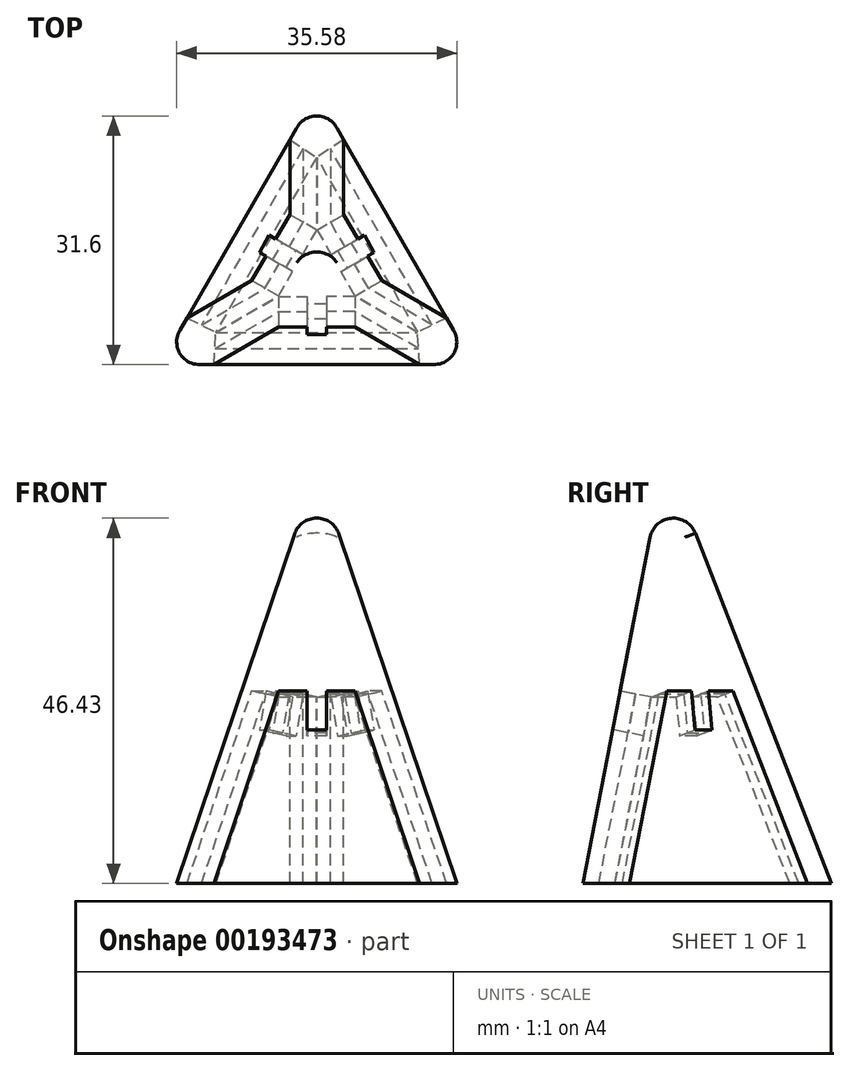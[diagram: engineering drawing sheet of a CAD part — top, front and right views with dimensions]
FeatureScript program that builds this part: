
annotation { "Feature Type Name" : "Feature", "Feature Type Description" : "" }
export const myFeature = defineFeature(function(context is Context, id is Id, definition is map)
    precondition{}
    {
        {
            var Q0;
            Q0=qCreatedBy(makeId("Top.planeOp"),FACE);
            var sketch = newSketch(context, id + "F13", { "sketchPlane" : qUnion([Q0])});
            skLineSegment(sketch, "E0", {"start": v(0, 21.94) * mm, "end": v(-19, -10.97) * mm, "construction": true});
            skLineSegment(sketch, "E1", {"start": v(-19, -10.97) * mm, "end": v(19, -10.97) * mm, "construction": true});
            skLineSegment(sketch, "E2", {"start": v(19, -10.97) * mm, "end": v(0, 21.94) * mm, "construction": true});
            skLineSegment(sketch, "E3", {"start": v(0, 0) * mm, "end": v(0, 21.94) * mm, "construction": true});
            skLineSegment(sketch, "E4", {"start": v(0, 0) * mm, "end": v(19, -10.97) * mm, "construction": true});
            skLineSegment(sketch, "E5", {"start": v(0, 0) * mm, "end": v(-19, -10.97) * mm, "construction": true});
            skLineSegment(sketch, "E6.0", {"start": v(21.6, -12.47) * mm, "end": v(0, 24.94) * mm});
            skLineSegment(sketch, "E6.1", {"start": v(-21.6, -12.47) * mm, "end": v(21.6, -12.47) * mm});
            skLineSegment(sketch, "E6.2", {"start": v(0, 24.94) * mm, "end": v(-21.6, -12.47) * mm});
            skSolve(sketch);
        }
        {
            var Q0;
            Q0=makeQuery(id+"F13.imprint","IMPRINT",FACE,{"disambiguationData":[TD([[makeQuery(id+"F13.imprint","IMPRINT",EDGE,{"derivedFrom":sQuery(id+"F13.wireOp",EDGE,"E6.0")}),1.0]])]});
            extrude(context, id + "F0", {"entities" : qUnion([Q0]), "depth" : 70 * mm, "hasDraft" : true, "draftAngle" : 11 * degree, "draftPullDirection" : true});
        }
        {
            var Q0;
            Q0=makeQuery(id+"F0.opExtrude","SWEPT_FACE",FACE,{"disambiguationData":[OSD([sQuery(id+"F13.wireOp",EDGE,"E6.1")])]});
            var sketch = newSketch(context, id + "F1", { "sketchPlane" : qUnion([Q0])});
            skLineSegment(sketch, "E7", {"start": v(-14.75, -2.38) * mm, "end": v(-4.84, 27.62) * mm});
            skLineSegment(sketch, "E8", {"start": v(-4.84, 27.62) * mm, "end": v(-1.25, 27.62) * mm});
            skLineSegment(sketch, "E9", {"start": v(-1.25, 27.62) * mm, "end": v(-1.25, 22.62) * mm});
            skLineSegment(sketch, "E10", {"start": v(-1.25, 22.62) * mm, "end": v(0, 22.62) * mm});
            skLineSegment(sketch, "E11", {"start": v(0, 22.62) * mm, "end": v(0, -2.38) * mm, "construction": true});
            skLineSegment(sketch, "E12", {"start": v(0, -2.38) * mm, "end": v(-14.75, -2.38) * mm});
            skLineSegment(sketch, "E13.MirrorCS", {"start": v(1.25, 27.62) * mm, "end": v(1.25, 22.62) * mm});
            skLineSegment(sketch, "E14.MirrorCS", {"start": v(4.84, 27.62) * mm, "end": v(1.25, 27.62) * mm});
            skLineSegment(sketch, "E15.MirrorCS", {"start": v(14.75, -2.38) * mm, "end": v(4.84, 27.62) * mm});
            skLineSegment(sketch, "E16.MirrorCS", {"start": v(0, -2.38) * mm, "end": v(14.75, -2.38) * mm});
            skLineSegment(sketch, "E17.MirrorCS", {"start": v(1.25, 22.62) * mm, "end": v(0, 22.62) * mm});
            skSolve(sketch);
        }
        {
            var Q0;
            Q0=qCreatedBy(makeId("Front.planeOp"),FACE);
            var sketch = newSketch(context, id + "F2", { "sketchPlane" : qUnion([Q0])});
            skLineSegment(sketch, "E18", {"start": v(0, 0) * mm, "end": v(0, 66.06) * mm, "construction": true});
            skSolve(sketch);
        }
        {
            var Q0;
            Q0 = qSketchRegion(id + "F1", true);
            extrude(context, id + "F3", {"entities" : qUnion([Q0]), "operationType" : NewBodyOperationType.REMOVE, "oppositeDirection" : true, "depth" : 4 * mm});
        }
        {
            var Q0;
            Q0=makeQuery(id+"F0.opExtrude","SWEPT_FACE",FACE,{"disambiguationData":[OSD([sQuery(id+"F13.wireOp",EDGE,"E6.0")])]});
            var sketch = newSketch(context, id + "F4", { "sketchPlane" : qUnion([Q0])});
            skLineSegment(sketch, "E19", {"start": v(-14.4, -3.98) * mm, "end": v(-7.83, 26.92) * mm});
            skLineSegment(sketch, "E20", {"start": v(-7.83, 26.92) * mm, "end": v(-4.27, 27.32) * mm});
            skLineSegment(sketch, "E21", {"start": v(-4.27, 27.32) * mm, "end": v(-3.72, 22.35) * mm});
            skLineSegment(sketch, "E22", {"start": v(-3.72, 22.35) * mm, "end": v(-2.48, 22.48) * mm});
            skLineSegment(sketch, "E23", {"start": v(-2.48, 22.48) * mm, "end": v(0.26, -2.37) * mm, "construction": true});
            skLineSegment(sketch, "E24", {"start": v(0.26, -2.37) * mm, "end": v(-14.4, -3.98) * mm});
            skLineSegment(sketch, "E25.MirrorCS", {"start": v(-1.78, 27.6) * mm, "end": v(-1.23, 22.62) * mm});
            skLineSegment(sketch, "E26.MirrorCS", {"start": v(1.78, 27.98) * mm, "end": v(-1.78, 27.6) * mm});
            skLineSegment(sketch, "E27.MirrorCS", {"start": v(14.92, -0.75) * mm, "end": v(1.78, 27.98) * mm});
            skLineSegment(sketch, "E28.MirrorCS", {"start": v(0.26, -2.37) * mm, "end": v(14.92, -0.75) * mm});
            skLineSegment(sketch, "E29.MirrorCS", {"start": v(-1.23, 22.62) * mm, "end": v(-2.48, 22.48) * mm});
            skSolve(sketch);
        }
        {
            var Q0;
            Q0 = qSketchRegion(id + "F4", true);
            extrude(context, id + "F5", {"entities" : qUnion([Q0]), "operationType" : NewBodyOperationType.REMOVE, "oppositeDirection" : true, "depth" : 4 * mm});
        }
        {
            var Q0;
            Q0=makeQuery(id+"F0.opExtrude","SWEPT_FACE",FACE,{"disambiguationData":[OSD([sQuery(id+"F13.wireOp",EDGE,"E6.2")])]});
            var sketch = newSketch(context, id + "F6", { "sketchPlane" : qUnion([Q0])});
            skLineSegment(sketch, "E30", {"start": v(-14.92, -0.75) * mm, "end": v(-1.78, 27.98) * mm});
            skLineSegment(sketch, "E31", {"start": v(-1.78, 27.98) * mm, "end": v(1.78, 27.6) * mm});
            skLineSegment(sketch, "E32", {"start": v(1.78, 27.6) * mm, "end": v(1.23, 22.62) * mm});
            skLineSegment(sketch, "E33", {"start": v(1.23, 22.62) * mm, "end": v(2.48, 22.48) * mm});
            skLineSegment(sketch, "E34", {"start": v(2.48, 22.48) * mm, "end": v(-0.26, -2.37) * mm, "construction": true});
            skLineSegment(sketch, "E35", {"start": v(-0.26, -2.37) * mm, "end": v(-14.92, -0.75) * mm});
            skLineSegment(sketch, "E36.MirrorCS", {"start": v(4.27, 27.32) * mm, "end": v(3.72, 22.35) * mm});
            skLineSegment(sketch, "E37.MirrorCS", {"start": v(7.83, 26.92) * mm, "end": v(4.27, 27.32) * mm});
            skLineSegment(sketch, "E38.MirrorCS", {"start": v(14.4, -3.98) * mm, "end": v(7.83, 26.92) * mm});
            skLineSegment(sketch, "E39.MirrorCS", {"start": v(-0.26, -2.37) * mm, "end": v(14.4, -3.98) * mm});
            skLineSegment(sketch, "E40.MirrorCS", {"start": v(3.72, 22.35) * mm, "end": v(2.48, 22.48) * mm});
            skSolve(sketch);
        }
        {
            var Q0;
            Q0 = qSketchRegion(id + "F6", true);
            extrude(context, id + "F7", {"entities" : qUnion([Q0]), "operationType" : NewBodyOperationType.REMOVE, "oppositeDirection" : true, "depth" : 4 * mm});
        }
        {
            var Q0;
            Q0 = qSketchRegion(id + "F1", true);
            extrude(context, id + "F8", {"entities" : qUnion([Q0]), "oppositeDirection" : true, "depth" : 2 * mm});
        }
        {
            var Q0;
            Q0=makeQuery(id+"F8.opExtrude","SWEPT_BODY",BODY,{"disambiguationData":[OSD([sQuery(id+"F1.wireOp",EDGE,"E7"),sQuery(id+"F1.wireOp",EDGE,"E8"),sQuery(id+"F1.wireOp",EDGE,"E9"),sQuery(id+"F1.wireOp",EDGE,"E10"),sQuery(id+"F1.wireOp",EDGE,"E12"),sQuery(id+"F1.wireOp",EDGE,"E13.MirrorCS"),sQuery(id+"F1.wireOp",EDGE,"E14.MirrorCS"),sQuery(id+"F1.wireOp",EDGE,"E15.MirrorCS"),sQuery(id+"F1.wireOp",EDGE,"E16.MirrorCS"),sQuery(id+"F1.wireOp",EDGE,"E17.MirrorCS")])]});
            var Q1;
            Q1=sQuery(id+"F2.wireOp",EDGE,"E18");
            circularPattern(context, id + "F9", {"entities" : qUnion([Q0]), "axis" : qUnion([Q1]), "angle" : 360 * degree, "instanceCount" : 3, "equalSpace" : true});
        }
        {
            var Q0;
            Q0=qCreatedBy(makeId("Right.planeOp"),FACE);
            var sketch = newSketch(context, id + "F10", { "sketchPlane" : qUnion([Q0])});
            skLineSegment(sketch, "E41.bottom", {"start": v(-14, 5) * mm, "end": v(26, 5) * mm});
            skLineSegment(sketch, "E41.top", {"start": v(-14, -1) * mm, "end": v(26, -1) * mm});
            skLineSegment(sketch, "E41.left", {"start": v(-14, 5) * mm, "end": v(-14, -1) * mm});
            skLineSegment(sketch, "E41.right", {"start": v(26, 5) * mm, "end": v(26, -1) * mm});
            skSolve(sketch);
        }
        {
            var Q0;
            Q0=makeQuery(id+"F10.imprint","IMPRINT",FACE,{"disambiguationData":[TD([[makeQuery(id+"F10.imprint","IMPRINT",EDGE,{"derivedFrom":sQuery(id+"F10.wireOp",EDGE,"E41.bottom")}),-1.0]])]});
            extrude(context, id + "F11", {"entities" : qUnion([Q0]), "operationType" : NewBodyOperationType.REMOVE, "oppositeDirection" : true, "depth" : 25 * mm, "hasSecondDirection" : true, "secondDirectionOppositeDirection" : false, "secondDirectionDepth" : 25 * mm});
        }
        {
            var Q0;
            Q0=makeQuery(id+"F0.opExtrude","SWEPT_EDGE",EDGE,{"disambiguationData":[OSD([sQuery(id+"F13.wireOp",EDGE,"E6.1"),sQuery(id+"F13.wireOp",EDGE,"E6.2")])]});
            var Q1;
            Q1=makeQuery(id+"F0.opExtrude","SWEPT_EDGE",EDGE,{"disambiguationData":[OSD([sQuery(id+"F13.wireOp",EDGE,"E6.0"),sQuery(id+"F13.wireOp",EDGE,"E6.1")])]});
            var Q2;
            Q2=makeQuery(id+"F0.opExtrude","SWEPT_EDGE",EDGE,{"disambiguationData":[OSD([sQuery(id+"F13.wireOp",EDGE,"E6.0"),sQuery(id+"F13.wireOp",EDGE,"E6.2")])]});
            fillet(context, id + "F12", {"entities" : qUnion([Q0, Q1, Q2]), "radius" : 3 * mm, "tangentPropagation" : true, "allowEdgeOverflow" : false});
        }
    });
